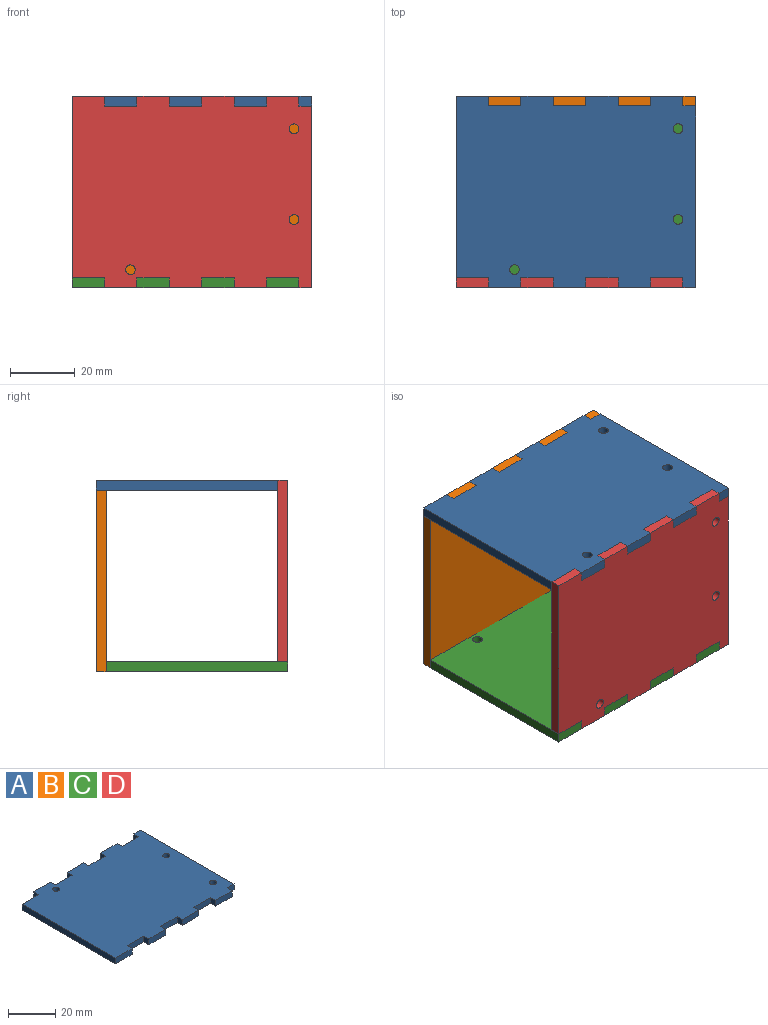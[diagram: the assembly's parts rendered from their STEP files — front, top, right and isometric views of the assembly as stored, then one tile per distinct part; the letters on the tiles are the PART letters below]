
ASSEMBLY  parts=4 mates=3
PART A: 37 faces, bbox 74x59x3 mm
  f0: plane 10x3mm, normal (0,1,0), area 30mm2, adj f1,f31,f32,f33
  f1: plane 56x3mm, normal (-1,0,0), area 168mm2, adj f0,f2,f32,f33
  f2: plane 10x3mm, normal (0,-1,0), area 30mm2, adj f1,f3,f32,f33
  f3: plane 3x3mm, normal (1,0,0), area 9mm2, adj f2,f4,f32,f33
  f4: plane 10x3mm, normal (0,-1,0), area 30mm2, adj f3,f5,f32,f33
  f5: plane 3x3mm, normal (-1,0,0), area 9mm2, adj f4,f6,f32,f33
  f6: plane 10x3mm, normal (0,-1,0), area 30mm2, adj f5,f7,f32,f33
  f7: plane 3x3mm, normal (1,0,0), area 9mm2, adj f6,f8,f32,f33
  f8: plane 10x3mm, normal (0,-1,0), area 30mm2, adj f7,f9,f32,f33
  f9: plane 3x3mm, normal (-1,0,0), area 9mm2, adj f8,f10,f32,f33
  f10: plane 10x3mm, normal (0,-1,0), area 30mm2, adj f9,f11,f32,f33
  f11: plane 3x3mm, normal (1,0,0), area 9mm2, adj f10,f12,f32,f33
  f12: plane 10x3mm, normal (0,-1,0), area 30mm2, adj f11,f13,f32,f33
  f13: plane 3x3mm, normal (-1,0,0), area 9mm2, adj f12,f14,f32,f33
  f14: plane 10x3mm, normal (0,-1,0), area 30mm2, adj f13,f15,f32,f33
  f15: plane 3x3mm, normal (1,0,0), area 9mm2, adj f14,f16,f32,f33
  f16: plane 4x3mm, normal (0,-1,0), area 12mm2, adj f15,f17,f32,f33
  f17: plane 56x3mm, normal (1,0,0), area 168mm2, adj f16,f18,f32,f33
  f18: plane 4x3mm, normal (0,1,0), area 12mm2, adj f17,f19,f32,f33
  f19: plane 3x3mm, normal (-1,0,0), area 9mm2, adj f18,f20,f32,f33
  f20: plane 10x3mm, normal (0,1,0), area 30mm2, adj f19,f21,f32,f33
  f21: plane 3x3mm, normal (1,0,0), area 9mm2, adj f20,f22,f32,f33
  f22: plane 10x3mm, normal (0,1,0), area 30mm2, adj f21,f23,f32,f33
  f23: plane 3x3mm, normal (-1,0,0), area 9mm2, adj f22,f24,f32,f33
  f24: plane 10x3mm, normal (0,1,0), area 30mm2, adj f23,f25,f32,f33
  f25: plane 3x3mm, normal (1,0,0), area 9mm2, adj f24,f26,f32,f33
  f26: plane 10x3mm, normal (0,1,0), area 30mm2, adj f25,f27,f32,f33
  f27: plane 3x3mm, normal (-1,0,0), area 9mm2, adj f26,f28,f32,f33
  f28: plane 10x3mm, normal (0,1,0), area 30mm2, adj f27,f29,f32,f33
  f29: plane 3x3mm, normal (1,0,0), area 9mm2, adj f28,f30,f32,f33
  f30: plane 10x3mm, normal (0,1,0), area 30mm2, adj f29,f31,f32,f33
  f31: plane 3x3mm, normal (-1,0,0), area 9mm2, adj f0,f30,f32,f33
  f32: plane 74x59mm, normal (0,0,1), area 4122.8mm2, adj f0,f1,f2,f3,f4,f5,f6,f7
  f33: plane 74x59mm, normal (0,0,-1), area 4122.8mm2, adj f0,f1,f2,f3,f4,f5,f6,f7
  f34: cylinder r=1.5mm len=3mm, axis (0,0,1), area 28.3mm2, adj f32,f33
  f35: cylinder r=1.5mm len=3mm, axis (0,0,1), area 28.3mm2, adj f32,f33
  f36: cylinder r=1.5mm len=3mm, axis (0,0,1), area 28.3mm2, adj f32,f33
PART B: same geometry as A
PART C: same geometry as A
PART D: same geometry as A
PLACE A rot(axis=(-1,0,0),180deg) t=(-30.56,20.4,112.92)mm
PLACE B rot(axis=(1,0,0),90deg) t=(-30.56,49.9,83.42)mm
PLACE C t=(-30.56,20.4,53.92)mm
PLACE D rot(axis=(-1,0,0),90deg) t=(-30.56,-9.1,83.42)mm
MATE fastened D.f29 <-> C.f5  axis (1,0,0) through (-47.56,-7.6,55.42)mm
MATE fastened D.f3 <-> A.f31  axis (1,0,0) through (-57.56,-7.6,111.42)mm
MATE fastened B.f27 <-> A.f7  axis (-1,0,0) through (-37.56,48.4,111.42)mm
